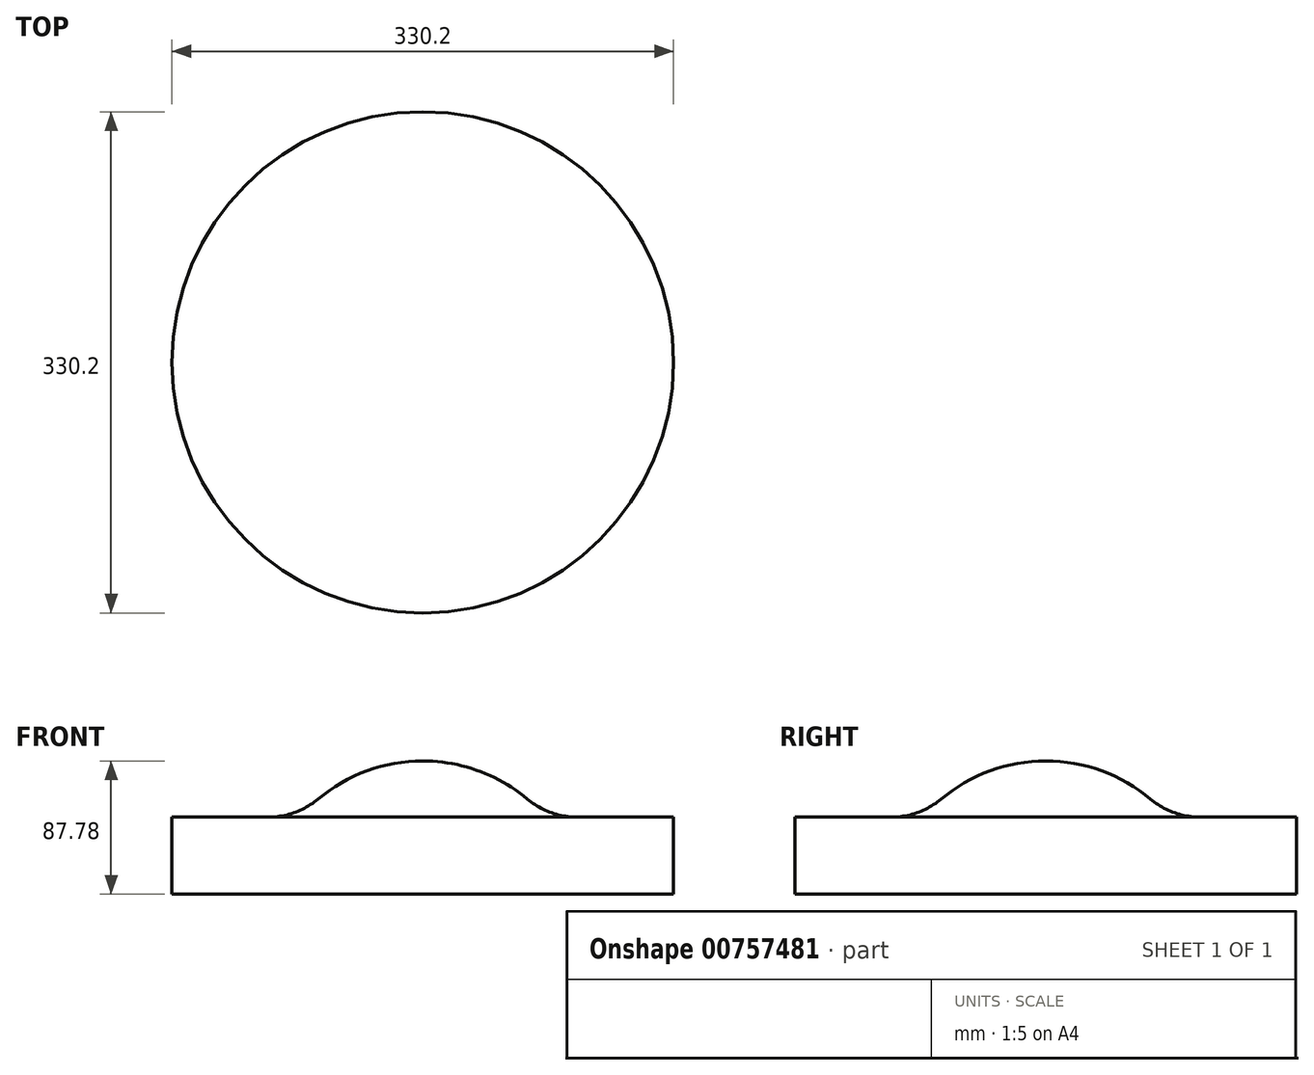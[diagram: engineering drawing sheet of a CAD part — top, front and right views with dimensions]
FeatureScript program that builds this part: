
annotation { "Feature Type Name" : "Feature", "Feature Type Description" : "" }
export const myFeature = defineFeature(function(context is Context, id is Id, definition is map)
    precondition{}
    {
        {
            var Q0;
            Q0=qCreatedBy(makeId("Front.planeOp"),FACE);
            var sketch = newSketch(context, id + "F0", { "sketchPlane" : qUnion([Q0])});
            skLineSegment(sketch, "E0", {"start": v(0, -50.8) * mm, "end": v(-165.1, -50.8) * mm});
            skLineSegment(sketch, "E1", {"start": v(-165.1, -50.8) * mm, "end": v(-165.1, 0) * mm});
            skLineSegment(sketch, "E2", {"start": v(-165.1, 0) * mm, "end": v(-101.6, 0) * mm});
            skArc(sketch, "E3", {"start": v(-101.6, 0) * mm, "mid": v(-84.23, 3.06) * mm, "end": v(-68.95, 11.88) * mm});
            skArc(sketch, "E4", {"start": v(-68.95, 11.88) * mm, "mid": v(-36.69, 30.51) * mm, "end": v(0, 36.98) * mm});
            skLineSegment(sketch, "E5", {"start": v(0, 36.98) * mm, "end": v(0, -50.8) * mm});
            skLineSegment(sketch, "E6", {"start": v(-68.95, 11.88) * mm, "end": v(0, 69.74) * mm, "construction": true});
            skSolve(sketch);
        }
        {
            var Q0;
            Q0 = qSketchRegion(id + "F0", true);
            var Q1;
            Q1=sQuery(id+"F0.wireOp",EDGE,"E5");
            revolve(context, id + "F1", {"surfaceOperationType" : NewSurfaceOperationType.NEW, "entities" : qUnion([Q0]), "axis" : qUnion([Q1]), "revolveType" : RevolveType.FULL});
        }
    });
